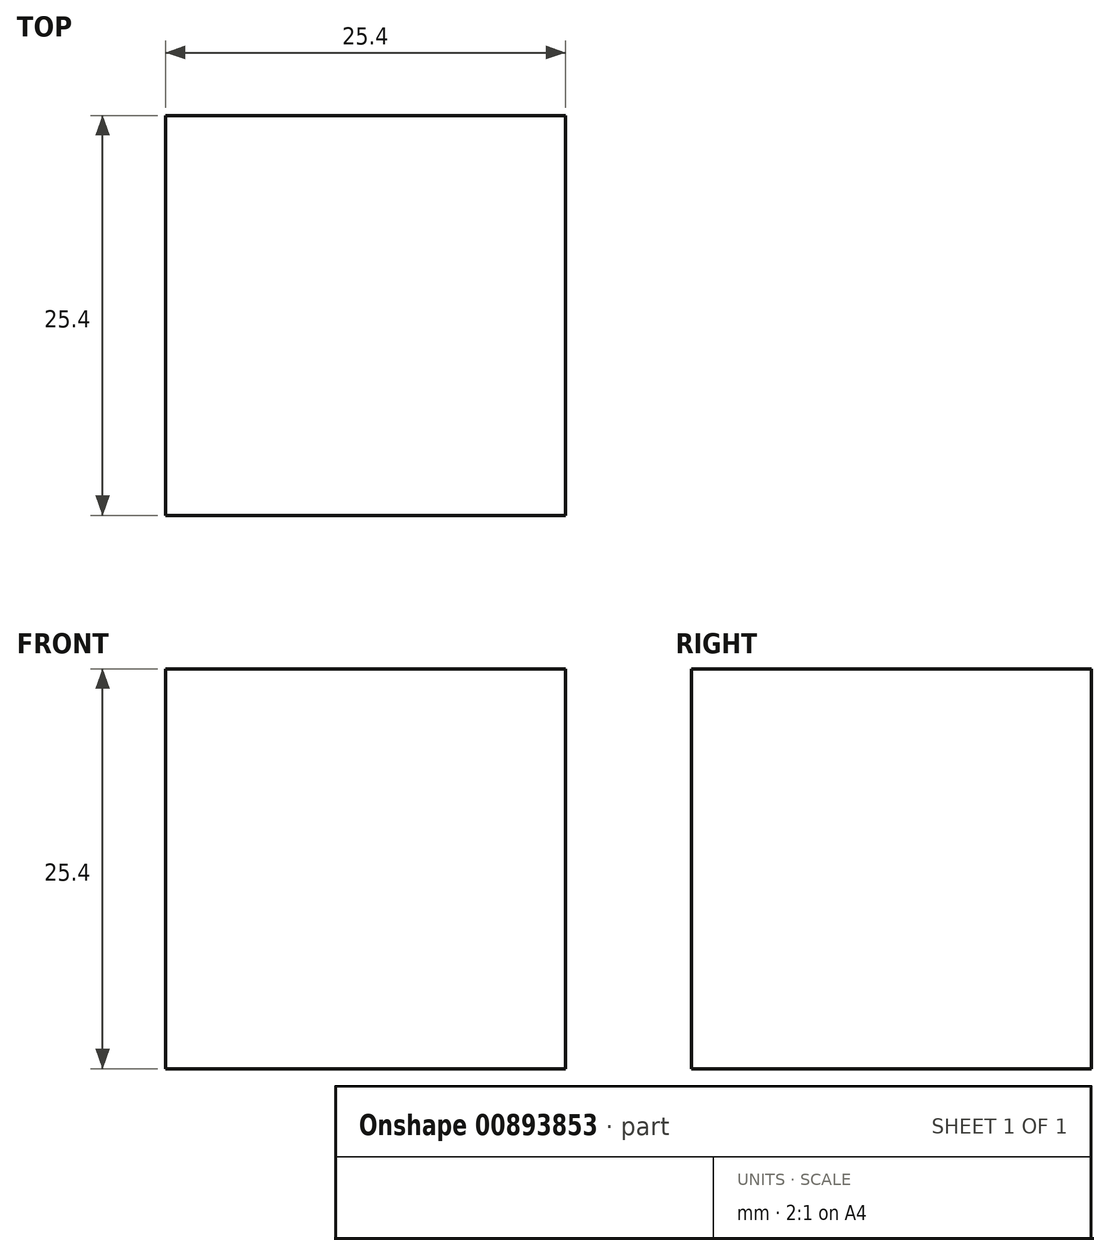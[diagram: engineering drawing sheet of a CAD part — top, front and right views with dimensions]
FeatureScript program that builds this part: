
annotation { "Feature Type Name" : "Feature", "Feature Type Description" : "" }
export const myFeature = defineFeature(function(context is Context, id is Id, definition is map)
    precondition{}
    {
        {
            var Q0;
            Q0=qCreatedBy(makeId("Front.planeOp"),FACE);
            var sketch = newSketch(context, id + "F0", { "sketchPlane" : qUnion([Q0])});
            skLineSegment(sketch, "E0", {"start": v(0, 0) * mm, "end": v(0, 25.4) * mm});
            skLineSegment(sketch, "E1", {"start": v(0, 25.4) * mm, "end": v(25.4, 25.4) * mm});
            skLineSegment(sketch, "E2", {"start": v(25.4, 25.4) * mm, "end": v(25.4, 0) * mm});
            skLineSegment(sketch, "E3", {"start": v(25.4, 0) * mm, "end": v(0, 0) * mm});
            skSolve(sketch);
        }
        {
            var Q0;
            Q0=qSketchRegion(id+"F0",true);
            extrude(context, id + "F1", {"entities" : qUnion([Q0]), "depth" : 25.4 * mm, "offsetDistance" : 25.4 * mm});
        }
    });
